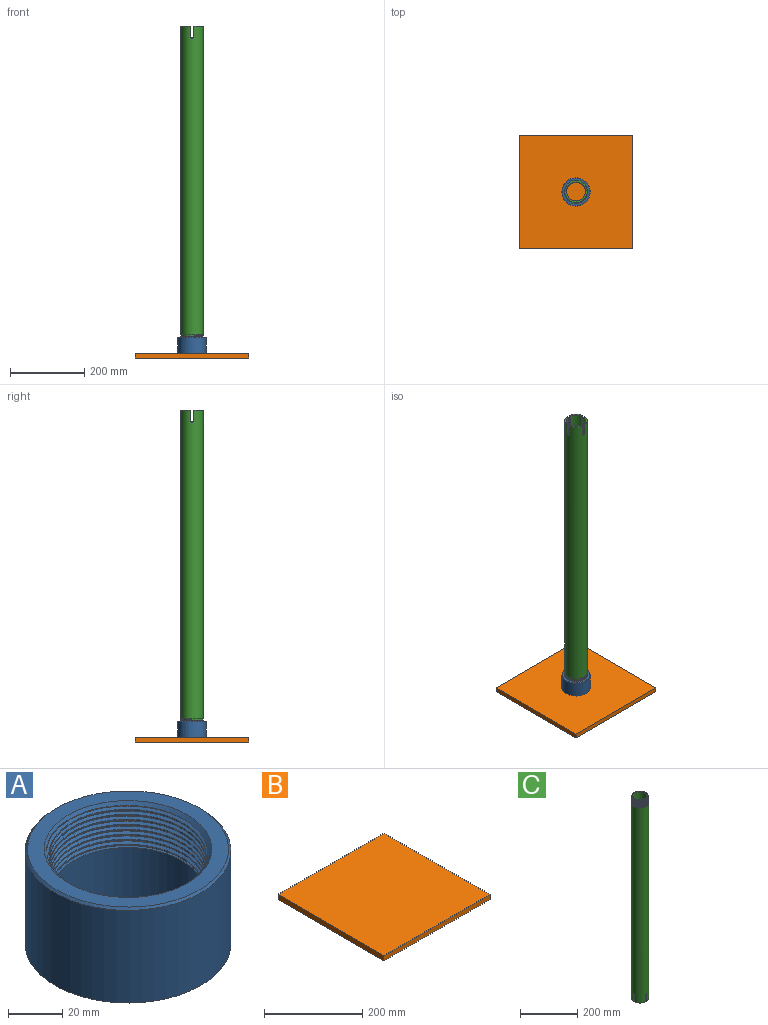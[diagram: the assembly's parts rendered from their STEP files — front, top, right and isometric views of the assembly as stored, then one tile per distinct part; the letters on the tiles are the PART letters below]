
ASSEMBLY  parts=3 mates=1
PART A: 11 faces, bbox 76.7x76.7x46.2 mm
  f0: cylinder r=28.13mm len=56.26mm, axis (0,0,1), area 4179.5mm2, adj f1,f10
  f1: plane 76.2x76.2mm, normal (0,0,-1), area 2074.5mm2, adj f0,f2
  f2: cylinder r=38.1mm len=76.2mm, axis (0,0,-1), area 10049.3mm2, adj f1,f3
  f3: cone r=37.22mm half-angle=45deg, axis (0,0,-1), area 295.6mm2, adj f2,f4
  f4: plane 74.43x74.43mm, normal (0,0,1), area 1323.3mm2, adj f3,f5
  f5: cone r=31.05mm half-angle=45deg, axis (0,0,1), area 423mm2, adj f4,f6,f7,f8,f9
  f6: bspline ~58.56x58.46mm, area 832.3mm2, adj f5,f7,f9,f10
  f7: bspline ~60.93x60.83mm, area 1095.1mm2, adj f5,f6,f8,f10
  f8: cone r=30.16mm half-angle=1.8deg, axis (0,0,1), area 478.1mm2, adj f5,f7,f9,f10
  f9: bspline ~60.18x53.1mm, area 9263.5mm2, adj f5,f6,f8,f10
  f10: plane 58.58x58.38mm, normal (0,0,1), area 143.1mm2, adj f0,f6,f7,f8,f9
PART B: 6 faces, bbox 304.8x304.8x12.7 mm
  f0: plane 304.8x12.7mm, normal (0,1,0), area 3871mm2, adj f1,f3,f4,f5
  f1: plane 304.8x12.7mm, normal (-1,0,0), area 3871mm2, adj f0,f2,f4,f5
  f2: plane 304.8x12.7mm, normal (0,-1,0), area 3871mm2, adj f1,f3,f4,f5
  f3: plane 304.8x12.7mm, normal (1,0,0), area 3871mm2, adj f0,f2,f4,f5
  f4: plane 304.8x304.8mm, normal (0,0,1), area 92903mm2, adj f0,f1,f2,f3
  f5: plane 304.8x304.8mm, normal (0,0,-1), area 92903mm2, adj f0,f1,f2,f3
PART C: 29 faces, bbox 60.5x60.4x869 mm
  f0: plane 25.93x25.93mm, normal (0,0,-1), area 169.9mm2, adj f2,f3,f11,f18
  f1: plane 25.93x25.93mm, normal (0,0,-1), area 169.9mm2, adj f2,f3,f9,f13
  f2: cylinder r=25.4mm len=863.6mm, axis (0,0,-1), area 136814.1mm2, adj f0,f1,f4,f5,f6,f7,f8,f9
  f3: cylinder r=30.16mm len=831.85mm, axis (0,0,-1), area 156640.3mm2, adj f0,f1,f4,f5,f7,f8,f9,f10
  f4: plane 25.93x25.93mm, normal (0,0,-1), area 169.9mm2, adj f2,f3,f12,f14
  f5: plane 25.93x25.93mm, normal (0,0,-1), area 169.9mm2, adj f2,f3,f8,f17
  f6: plane 55.41x55.33mm, normal (0,0,1), area 378.1mm2, adj f2,f24,f26,f27,f28
  f7: cylinder r=3.97mm len=7.94mm, axis (1,0,0), area 59.7mm2, adj f2,f3,f8,f9
  f8: plane 28.58x4.81mm, normal (0,1,0), area 137.5mm2, adj f2,f3,f5,f7
  f9: plane 28.58x4.81mm, normal (0,-1,0), area 137.5mm2, adj f1,f2,f3,f7
  f10: cylinder r=3.97mm len=7.94mm, axis (-1,0,0), area 59.7mm2, adj f2,f3,f11,f12
  f11: plane 28.58x4.81mm, normal (0,1,0), area 137.5mm2, adj f0,f2,f3,f10
  f12: plane 28.58x4.81mm, normal (0,-1,0), area 137.5mm2, adj f2,f3,f4,f10
  f13: plane 28.58x4.81mm, normal (1,0,0), area 137.5mm2, adj f1,f2,f3,f15
  f14: plane 28.58x4.81mm, normal (-1,0,0), area 137.5mm2, adj f2,f3,f4,f15
  f15: cylinder r=3.97mm len=7.94mm, axis (0,-1,0), area 59.7mm2, adj f2,f3,f13,f14
  f16: cylinder r=3.97mm len=7.94mm, axis (0,1,0), area 59.7mm2, adj f2,f3,f17,f18
  f17: plane 28.58x4.81mm, normal (1,0,0), area 137.5mm2, adj f2,f3,f5,f16
  f18: plane 28.58x4.81mm, normal (-1,0,0), area 137.5mm2, adj f0,f2,f3,f16
  f19: cone r=28.18mm half-angle=3.6deg, axis (0,0,-1), area 631.6mm2, adj f3,f20,f25,f26,f28
  f20: cone r=28.18mm half-angle=3.6deg, axis (0,0,-1), area 171.5mm2, adj f19,f21,f26,f28
  f21: cone r=28.18mm half-angle=3.6deg, axis (0,0,-1), area 168.6mm2, adj f20,f22,f26,f28
  f22: cone r=28.18mm half-angle=3.6deg, axis (0,0,-1), area 166.7mm2, adj f21,f23,f26,f28
  f23: cone r=28.18mm half-angle=3.6deg, axis (0,0,-1), area 164.6mm2, adj f22,f24,f26,f28
  f24: cone r=28.18mm half-angle=3.6deg, axis (0,0,-1), area 36.2mm2, adj f6,f23,f26,f28
  f25: plane 4.77x1.38mm, normal (0,1,0), area 2.9mm2, adj f19,f26,f27,f28
  f26: bspline ~60.47x60.38mm, area 2090mm2, adj f6,f19,f20,f21,f22,f23,f24,f25
  f27: bspline ~60.47x60.38mm, area 2915.8mm2, adj f6,f25,f26,f28
  f28: bspline ~60.47x60.38mm, area 59.1mm2, adj f6,f19,f20,f21,f22,f23,f24,f25
PLACE A rot(axis=(0,0,1),0deg) t=(27.82,-17.43,-22.45)mm
PLACE B t=(-56.36,74.23,-56.58)mm
PLACE C rot(axis=(0,1,0),180deg) t=(27.82,-17.43,838.77)mm
MATE planar A.f0 <-> B.f4  axis (0,0,-1) through (27.82,-17.43,-43.88)mm
